# Revit family: Hager-Panelboards-Surface_mounted-IP3X-With_Cover-Hosted-GB-en
name_source: partatom
category: Electrical Equipment
units: mm (PartAtom-declared; Revit-internal decimal feet)

## family parameters
Cut with Voids When Loaded = No
Host = Face
Maintain Annotation Orientation = Yes
Panel Configuration = Two Columns, Circuits Across
Part Type = Panelboard
Room Calculation Point = No
Round Connector Dimension = Use Diameter
Shared = No

## types (58) — shared parameters
BC_MODEL_ID = 1554496
BC_OBJECT_ID = 513947
BC_OBJECT_VERSION = #1
Classification.Uniclass.Pr.Description = Control circuit device enclosures
Classification.Uniclass.Pr.Number = Pr_80_77_28_16
Code hager = ADD-EC000214_UKVR
EF000003 - Mounting method = Surface mounted
EF000007 - Colour = Grey
EF000024 - UV resistant = No
EF000116 - RAL number = 7035
EF000118 - With mounting plate = No
EF000218 - Built-in depth = 150 mm
EF000332 - Built-in height = 450 mm  [stored 1.47638 ft]
EF000846 - Built-in width = 450 mm  [stored 1.47638 ft]
EF001062 - EMC-version = No
EF001088 - Extension possible = Yes
EF001134 - DIN-rail = Yes
EF001134 - With DIN-rail = No
EF001596 - Housing material = Steel
EF005474 - Degree of protection (IP rating) = IP3X
EF006306 - With lock = Yes
EF015776 - Earthing terminal block = Yes
EF015777 - Neutral terminal block = Yes
EF015941 - Signal passing door = No
ETIM class code = EC000214
ETIM class name = Small distribution board
HG000002-With door or cover = Yes
HG000003-Range = Panelboards
HG000005-Thickness = 3 mm  [stored 0.00984252 ft]
HG000006-Flush mounted = No
HG000017-Distance between poles = 25 mm  [stored 0.082021 ft]
HG000060-RAL-number = 7035
HG000099-Onfly Template ID = 507572
Manufacturer = Hager
Name = Panelboards-Surface_mounted-IP3X-With_Cover-GB
Name BIM&CO = Electricity
Name hager = ADD_Enclosures_EC000214
Type Comments = Panelboards
Uniformat = Low Tension Service & Dist.
Uniformat code = D501001
zero-valued in all types: Default Elevation, EF000218 - Recess depth, EF000266 - Number of rows, EF000332 - Recess height, EF000846 - Recess width, EF001131 - Internal depth

## per-type parameters (varying)
| type | BC_VARIANT_ID | EF000008 - Width | EF000040 - Height | EF000049 - Depth | EF002950 - Width in number of modular spacings | EF006244 - Transparent cover/door | HG000004-Manufacturer reference | HGEF000266-Number of rows | HGEF002950-Width in number of modular spacings | Model |
| Panelboards-Surface_mounted_W900_H1250_D220_9_Modular_Spacing-JF406B | 1179363 | 900 mm  [stored 2.95276 ft] | 1250 mm  [stored 4.10105 ft] | 220 mm  [stored 0.721785 ft] | 9 | No | JF406B | 1 | 16 | JF406B |
| Panelboards-Surface_mounted_W900_H1250_D220_9_Modular_Spacing-JF406BG | 1179364 | 900 mm  [stored 2.95276 ft] | 1250 mm  [stored 4.10105 ft] | 220 mm  [stored 0.721785 ft] | 9 | Yes | JF406BG | 0 | 0 | JF406BG |
| Panelboards-Surface_mounted_W900_H1250_D220_12_Modular_Spacing-JF408B | 1179365 | 900 mm  [stored 2.95276 ft] | 1250 mm  [stored 4.10105 ft] | 220 mm  [stored 0.721785 ft] | 12 | No | JF408B | 0 | 0 | JF408B |
| Panelboards-Surface_mounted_W900_H1250_D220_12_Modular_Spacing-JF408BG | 1179366 | 900 mm  [stored 2.95276 ft] | 1250 mm  [stored 4.10105 ft] | 220 mm  [stored 0.721785 ft] | 12 | Yes | JF408BG | 0 | 0 | JF408BG |
| Panelboards-Surface_mounted_W900_H1400_D220_18_Modular_Spacing-JF412B | 1179367 | 900 mm  [stored 2.95276 ft] | 1400 mm  [stored 4.59318 ft] | 220 mm  [stored 0.721785 ft] | 18 | No | JF412B | 0 | 0 | JF412B |
| Panelboards-Surface_mounted_W900_H1400_D220_18_Modular_Spacing-JF412BG | 1179368 | 900 mm  [stored 2.95276 ft] | 1400 mm  [stored 4.59318 ft] | 220 mm  [stored 0.721785 ft] | 18 | Yes | JF412BG | 1 | 16 | JF412BG |
| Panelboards-Surface_mounted_W900_H1550_D220_24_Modular_Spacing-JF416B | 1179369 | 900 mm  [stored 2.95276 ft] | 1550 mm  [stored 5.0853 ft] | 220 mm  [stored 0.721785 ft] | 24 | No | JF416B | 1 | 16 | JF416B |
| Panelboards-Surface_mounted_W900_H1550_D220_24_Modular_Spacing-JF416BG | 1179370 | 900 mm  [stored 2.95276 ft] | 1550 mm  [stored 5.0853 ft] | 220 mm  [stored 0.721785 ft] | 24 | Yes | JF416BG | 2 | 16 | JF416BG |
| Panelboards-Surface_mounted_W900_H1700_D220_27_Modular_Spacing-JF418B | 1179371 | 900 mm  [stored 2.95276 ft] | 1700 mm  [stored 5.57743 ft] | 220 mm  [stored 0.721785 ft] | 27 | No | JF418B | 2 | 16 | JF418B |
| Panelboards-Surface_mounted_W900_H1700_D220_27_Modular_Spacing-JF418BG | 1179372 | 900 mm  [stored 2.95276 ft] | 1700 mm  [stored 5.57743 ft] | 220 mm  [stored 0.721785 ft] | 27 | Yes | JF418BG | 2 | 16 | JF418BG |
| Panelboards-Surface_mounted_W900_H1250_D220_9_Modular_Spacing-JF60204B | 1179373 | 900 mm  [stored 2.95276 ft] | 1250 mm  [stored 4.10105 ft] | 220 mm  [stored 0.721785 ft] | 9 | No | JF60204B | 2 | 16 | JF60204B |
| Panelboards-Surface_mounted_W900_H1250_D220_9_Modular_Spacing-JF60204BG | 1179374 | 900 mm  [stored 2.95276 ft] | 1250 mm  [stored 4.10105 ft] | 220 mm  [stored 0.721785 ft] | 9 | Yes | JF60204BG | 3 | 16 | JF60204BG |
| Panelboards-Surface_mounted_W900_H1250_D220_12_Modular_Spacing-JF608B | 1179375 | 900 mm  [stored 2.95276 ft] | 1250 mm  [stored 4.10105 ft] | 220 mm  [stored 0.721785 ft] | 12 | No | JF608B | 4 | 16 | JF608B |
| Panelboards-Surface_mounted_W900_H1250_D220_12_Modular_Spacing-JF608BG | 1179376 | 900 mm  [stored 2.95276 ft] | 1250 mm  [stored 4.10105 ft] | 220 mm  [stored 0.721785 ft] | 12 | Yes | JF608BG | 5 | 16 | JF608BG |
| Panelboards-Surface_mounted_W900_H1250_D220_0_Modular_Spacing-JF80204B | 1179377 | 900 mm  [stored 2.95276 ft] | 1250 mm  [stored 4.10105 ft] | 220 mm  [stored 0.721785 ft] | 0 | No | JF80204B | 6 | 16 | JF80204B |
| Panelboards-Surface_mounted_W900_H1250_D220_0_Modular_Spacing-JF80204BG | 1179378 | 900 mm  [stored 2.95276 ft] | 1250 mm  [stored 4.10105 ft] | 220 mm  [stored 0.721785 ft] | 0 | Yes | JF80204BG | 1 | 16 | JF80204BG |
| Panelboards-Surface_mounted_W900_H1250_D220_12_Modular_Spacing-JF80206B | 1179379 | 900 mm  [stored 2.95276 ft] | 1250 mm  [stored 4.10105 ft] | 220 mm  [stored 0.721785 ft] | 12 | No | JF80206B | 2 | 16 | JF80206B |
| Panelboards-Surface_mounted_W900_H1250_D220_12_Modular_Spacing-JF80206BG | 1179380 | 900 mm  [stored 2.95276 ft] | 1250 mm  [stored 4.10105 ft] | 220 mm  [stored 0.721785 ft] | 12 | Yes | JF80206BG | 0 | 0 | JF80206BG |
| Panelboards-Surface_mounted_W900_H1400_D220_18_Modular_Spacing-JF80210B | 1179381 | 900 mm  [stored 2.95276 ft] | 1400 mm  [stored 4.59318 ft] | 220 mm  [stored 0.721785 ft] | 18 | No | JF80210B | 3 | 12 | JF80210B |
| Panelboards-Surface_mounted_W900_H1400_D220_18_Modular_Spacing-JF80210BG | 1179382 | 900 mm  [stored 2.95276 ft] | 1400 mm  [stored 4.59318 ft] | 220 mm  [stored 0.721785 ft] | 18 | Yes | JF80210BG | 3 | 24 | JF80210BG |
| Panelboards-Surface_mounted_W900_H1250_D220_12_Modular_Spacing-JF80404B | 1179383 | 900 mm  [stored 2.95276 ft] | 1250 mm  [stored 4.10105 ft] | 220 mm  [stored 0.721785 ft] | 12 | No | JF80404B | 4 | 12 | JF80404B |
| Panelboards-Surface_mounted_W900_H1250_D220_12_Modular_Spacing-JF80404BG | 1179384 | 900 mm  [stored 2.95276 ft] | 1250 mm  [stored 4.10105 ft] | 220 mm  [stored 0.721785 ft] | 12 | Yes | JF80404BG | 4 | 24 | JF80404BG |
| Panelboards-Surface_mounted_W900_H1400_D220_18_Modular_Spacing-JF80408B | 1179385 | 900 mm  [stored 2.95276 ft] | 1400 mm  [stored 4.59318 ft] | 220 mm  [stored 0.721785 ft] | 18 | No | JF80408B | 4 | 36 | JF80408B |
| Panelboards-Surface_mounted_W900_H1400_D220_18_Modular_Spacing-JF80408BG | 1179386 | 900 mm  [stored 2.95276 ft] | 1400 mm  [stored 4.59318 ft] | 220 mm  [stored 0.721785 ft] | 18 | Yes | JF80408BG | 5 | 12 | JF80408BG |
| Panelboards-Surface_mounted_W900_H1700_D220_27_Modular_Spacing-JF80414B | 1179387 | 900 mm  [stored 2.95276 ft] | 1700 mm  [stored 5.57743 ft] | 220 mm  [stored 0.721785 ft] | 27 | No | JF80414B | 5 | 24 | JF80414B |
| Panelboards-Surface_mounted_W900_H1700_D220_27_Modular_Spacing-JF80414BG | 1179388 | 900 mm  [stored 2.95276 ft] | 1700 mm  [stored 5.57743 ft] | 220 mm  [stored 0.721785 ft] | 27 | Yes | JF80414BG | 5 | 36 | JF80414BG |
| Panelboards-Surface_mounted_W900_H1700_D220_27_Modular_Spacing-JF80612B | 1179389 | 900 mm  [stored 2.95276 ft] | 1700 mm  [stored 5.57743 ft] | 220 mm  [stored 0.721785 ft] | 27 | No | JF80612B | 6 | 12 | JF80612B |
| Panelboards-Surface_mounted_W900_H1700_D220_27_Modular_Spacing-JF80612BG | 1179390 | 900 mm  [stored 2.95276 ft] | 1700 mm  [stored 5.57743 ft] | 220 mm  [stored 0.721785 ft] | 27 | Yes | JF80612BG | 6 | 24 | JF80612BG |
| Panelboards-Surface_mounted_W900_H1400_D220_18_Modular_Spacing-JF812B | 1179391 | 900 mm  [stored 2.95276 ft] | 1400 mm  [stored 4.59318 ft] | 220 mm  [stored 0.721785 ft] | 18 | No | JF812B | 6 | 36 | JF812B |
| Panelboards-Surface_mounted_W900_H1400_D220_18_Modular_Spacing-JF812BG | 1179392 | 900 mm  [stored 2.95276 ft] | 1400 mm  [stored 4.59318 ft] | 220 mm  [stored 0.721785 ft] | 18 | Yes | JF812BG | 7 | 36 | JF812BG |
| Panelboards-Surface_mounted_W900_H1700_D220_27_Modular_Spacing-JF818B | 1179393 | 900 mm  [stored 2.95276 ft] | 1700 mm  [stored 5.57743 ft] | 220 mm  [stored 0.721785 ft] | 27 | No | JF818B | 4 | 24 | JF818B |
| Panelboards-Surface_mounted_W900_H1700_D220_27_Modular_Spacing-JF818BG | 1179394 | 900 mm  [stored 2.95276 ft] | 1700 mm  [stored 5.57743 ft] | 220 mm  [stored 0.721785 ft] | 27 | Yes | JF818BG | 4 | 26 | JF818BG |
| Panelboards-Surface_mounted_W900_H1900_D220_12_Modular_Spacing-JHF80206B | 1179395 | 900 mm  [stored 2.95276 ft] | 1900 mm  [stored 6.2336 ft] | 220 mm  [stored 0.721785 ft] | 12 | No | JHF80206B | 5 | 24 | JHF80206B |
| Panelboards-Surface_mounted_W900_H1900_D220_12_Modular_Spacing-JHF80206BG | 1179396 | 900 mm  [stored 2.95276 ft] | 1900 mm  [stored 6.2336 ft] | 220 mm  [stored 0.721785 ft] | 12 | Yes | JHF80206BG | 5 | 26 | JHF80206BG |
| Panelboards-Surface_mounted_W900_H2050_D220_18_Modular_Spacing-JHF80210B | 1179397 | 900 mm  [stored 2.95276 ft] | 2050 mm  [stored 6.72572 ft] | 220 mm  [stored 0.721785 ft] | 18 | No | JHF80210B | 6 | 24 | JHF80210B |
| Panelboards-Surface_mounted_W900_H2050_D220_18_Modular_Spacing-JHF80210BG | 1179398 | 900 mm  [stored 2.95276 ft] | 2050 mm  [stored 6.72572 ft] | 220 mm  [stored 0.721785 ft] | 18 | Yes | JHF80210BG | 6 | 26 | JHF80210BG |
| Panelboards-Surface_mounted_W900_H1900_D220_12_Modular_Spacing-JHF80404B | 1179399 | 900 mm  [stored 2.95276 ft] | 1900 mm  [stored 6.2336 ft] | 220 mm  [stored 0.721785 ft] | 12 | No | JHF80404B | 7 | 26 | JHF80404B |
| Panelboards-Surface_mounted_W900_H1900_D220_12_Modular_Spacing-JHF80404BG | 1179400 | 900 mm  [stored 2.95276 ft] | 1900 mm  [stored 6.2336 ft] | 220 mm  [stored 0.721785 ft] | 12 | Yes | JHF80404BG | 3 | 12 | JHF80404BG |
| Panelboards-Surface_mounted_W900_H2050_D220_18_Modular_Spacing-JHF80408B | 1179401 | 900 mm  [stored 2.95276 ft] | 2050 mm  [stored 6.72572 ft] | 220 mm  [stored 0.721785 ft] | 18 | No | JHF80408B | 3 | 24 | JHF80408B |
| Panelboards-Surface_mounted_W900_H2050_D220_18_Modular_Spacing-JHF80408BG | 1179402 | 900 mm  [stored 2.95276 ft] | 2050 mm  [stored 6.72572 ft] | 220 mm  [stored 0.721785 ft] | 18 | Yes | JHF80408BG | 4 | 12 | JHF80408BG |
| Panelboards-Surface_mounted_W900_H2200_D220_27_Modular_Spacing-JHF80414B | 1179403 | 900 mm  [stored 2.95276 ft] | 2200 mm | 220 mm  [stored 0.721785 ft] | 27 | No | JHF80414B | 4 | 24 | JHF80414B |
| Panelboards-Surface_mounted_W900_H2200_D220_27_Modular_Spacing-JHF80414BG | 1179404 | 900 mm  [stored 2.95276 ft] | 2200 mm | 220 mm  [stored 0.721785 ft] | 27 | Yes | JHF80414BG | 4 | 36 | JHF80414BG |
| Panelboards-Surface_mounted_W900_H2200_D220_27_Modular_Spacing-JHF80612B | 1179405 | 900 mm  [stored 2.95276 ft] | 2200 mm | 220 mm  [stored 0.721785 ft] | 27 | No | JHF80612B | 5 | 12 | JHF80612B |
| Panelboards-Surface_mounted_W900_H2200_D220_27_Modular_Spacing-JHF80612BG | 1179406 | 900 mm  [stored 2.95276 ft] | 2200 mm | 220 mm  [stored 0.721785 ft] | 27 | Yes | JHF80612BG | 5 | 24 | JHF80612BG |
| Panelboards-Surface_mounted_W900_H2050_D220_18_Modular_Spacing-JHF812B | 1179407 | 900 mm  [stored 2.95276 ft] | 2050 mm  [stored 6.72572 ft] | 220 mm  [stored 0.721785 ft] | 18 | No | JHF812B | 5 | 36 | JHF812B |
| Panelboards-Surface_mounted_W900_H2050_D220_18_Modular_Spacing-JHF812BG | 1179408 | 900 mm  [stored 2.95276 ft] | 2050 mm  [stored 6.72572 ft] | 220 mm  [stored 0.721785 ft] | 18 | Yes | JHF812BG | 6 | 12 | JHF812BG |
| Panelboards-Surface_mounted_W900_H2200_D220_27_Modular_Spacing-JHF818B | 1179409 | 900 mm  [stored 2.95276 ft] | 2200 mm | 220 mm  [stored 0.721785 ft] | 27 | No | JHF818B | 6 | 24 | JHF818B |
| Panelboards-Surface_mounted_W900_H2200_D220_27_Modular_Spacing-JHF818BG | 1179410 | 900 mm  [stored 2.95276 ft] | 2200 mm | 220 mm  [stored 0.721785 ft] | 27 | Yes | JHF818BG | 6 | 36 | JHF818BG |
| Panelboards-Surface_mounted_W710_H950_D160_6_Modular_Spacing-JN204B | 1179411 | 710 mm | 950 mm  [stored 3.1168 ft] | 160 mm  [stored 0.524934 ft] | 6 | No | JN204B | 7 | 36 | JN204B |
| Panelboards-Surface_mounted_W710_H950_D160_6_Modular_Spacing-JN204BG | 1179412 | 710 mm | 950 mm  [stored 3.1168 ft] | 160 mm  [stored 0.524934 ft] | 6 | Yes | JN204BG | 4 | 12 | JN204BG |
| Panelboards-Surface_mounted_W710_H1100_D160_9_Modular_Spacing-JN206B | 1179413 | 710 mm | 1100 mm | 160 mm  [stored 0.524934 ft] | 9 | No | JN206B | 4 | 12 | JN206B |
| Panelboards-Surface_mounted_W710_H1100_D160_9_Modular_Spacing-JN206BG | 1179414 | 710 mm | 1100 mm | 160 mm  [stored 0.524934 ft] | 9 | Yes | JN206BG | 4 | 12 | JN206BG |
| Panelboards-Surface_mounted_W710_H1100_D160_12_Modular_Spacing-JN208B | 1179415 | 710 mm | 1100 mm | 160 mm  [stored 0.524934 ft] | 12 | No | JN208B | 4 | 12 | JN208B |
| Panelboards-Surface_mounted_W710_H1100_D160_12_Modular_Spacing-JN208BG | 1179416 | 710 mm | 1100 mm | 160 mm  [stored 0.524934 ft] | 12 | Yes | JN208BG | 4 | 12 | JN208BG |
| Panelboards-Surface_mounted_W710_H1250_D160_0_Modular_Spacing-JN212B | 1179417 | 710 mm | 1250 mm  [stored 4.10105 ft] | 160 mm  [stored 0.524934 ft] | 0 | No | JN212B | 4 | 12 | JN212B |
| Panelboards-Surface_mounted_W710_H1250_D160_18_Modular_Spacing-JN212BG | 1179418 | 710 mm | 1250 mm  [stored 4.10105 ft] | 160 mm  [stored 0.524934 ft] | 18 | Yes | JN212BG | 4 | 12 | JN212BG |
| Panelboards-Surface_mounted_W710_H1550_D160_24_Modular_Spacing-JN216B | 1179419 | 710 mm | 1550 mm  [stored 5.0853 ft] | 160 mm  [stored 0.524934 ft] | 24 | No | JN216B | 4 | 12 | JN216B |
| Panelboards-Surface_mounted_W710_H1550_D160_24_Modular_Spacing-JN216BG | 1179420 | 710 mm | 1550 mm  [stored 5.0853 ft] | 160 mm  [stored 0.524934 ft] | 24 | Yes | JN216BG | 5 | 12 | JN216BG |

note: column(s) folded — value = type name in every type: Reference

note: [stored X ft] marks values corroborated as IEEE doubles in the binary element streams (Revit-internal decimal feet)

## geometry (parser evidence)
native form markers: Sweep x13
no freeform markers — native parametric forms only
